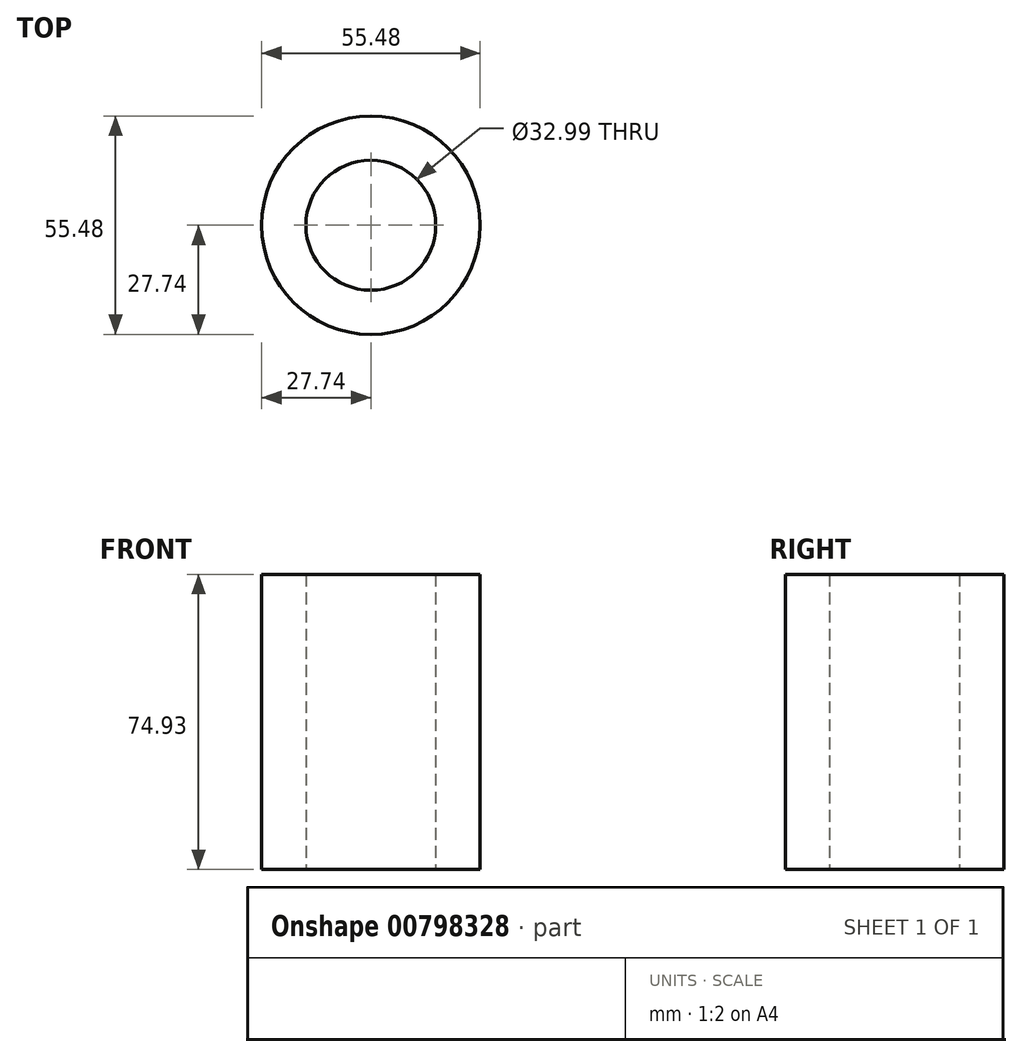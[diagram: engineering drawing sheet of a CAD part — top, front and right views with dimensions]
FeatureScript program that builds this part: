
annotation { "Feature Type Name" : "Feature", "Feature Type Description" : "" }
export const myFeature = defineFeature(function(context is Context, id is Id, definition is map)
    precondition{}
    {
        {
            var Q0;
            Q0=qCreatedBy(makeId("Top.planeOp"),FACE);
            var sketch = newSketch(context, id + "F0", { "sketchPlane" : qUnion([Q0])});
            skCircle(sketch, "E0", {"center": v(0, 0) * mm, "radius": 27.74 * mm});
            skCircle(sketch, "E1", {"center": v(0, 0) * mm, "radius": 16.5 * mm});
            skSolve(sketch);
        }
        {
            var Q0;
            Q0 = qSketchRegion(id + "F0", true);
            extrude(context, id + "F1", {"entities" : qUnion([Q0]), "depth" : 74.93 * mm, "offsetDistance" : 25.4 * mm});
        }
    });
